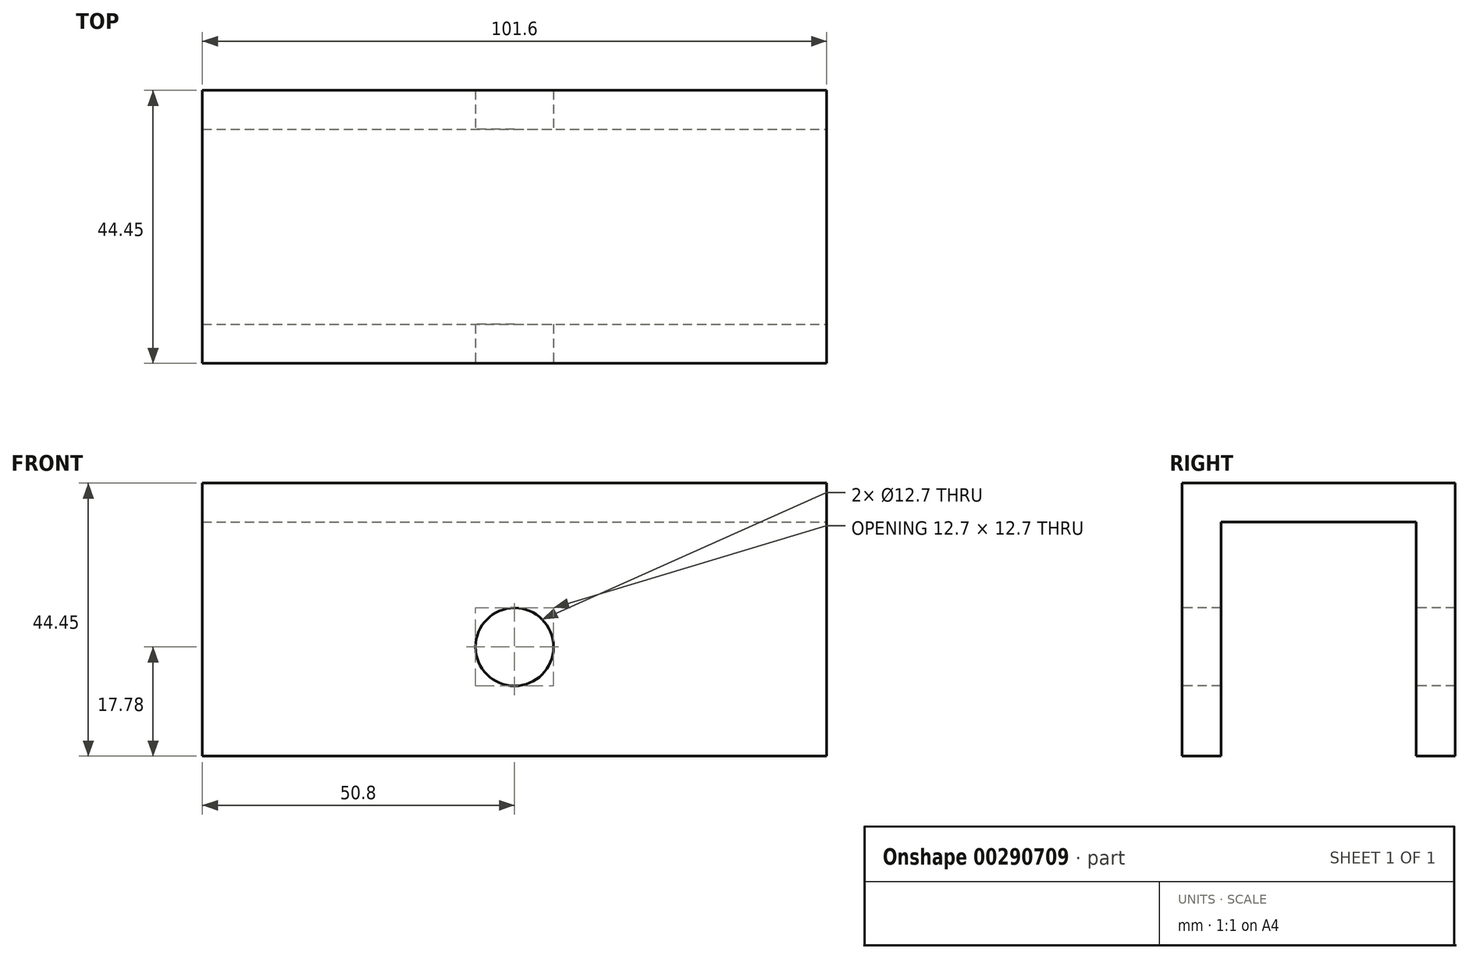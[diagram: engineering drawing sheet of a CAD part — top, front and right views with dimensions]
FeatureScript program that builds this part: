
annotation { "Feature Type Name" : "Feature", "Feature Type Description" : "" }
export const myFeature = defineFeature(function(context is Context, id is Id, definition is map)
    precondition{}
    {
        {
            var Q0;
            Q0=qCreatedBy(makeId("Front.planeOp"),FACE);
            var sketch = newSketch(context, id + "F0", { "sketchPlane" : qUnion([Q0])});
            skLineSegment(sketch, "E0.bottom", {"start": v(0, 0) * mm, "end": v(101.6, 0) * mm});
            skLineSegment(sketch, "E0.top", {"start": v(0, -44.45) * mm, "end": v(101.6, -44.45) * mm});
            skLineSegment(sketch, "E0.left", {"start": v(0, 0) * mm, "end": v(0, -44.45) * mm});
            skLineSegment(sketch, "E0.right", {"start": v(101.6, 0) * mm, "end": v(101.6, -44.45) * mm});
            skSolve(sketch);
        }
        {
            var Q0;
            Q0=makeQuery(id+"F0.imprint","IMPRINT",FACE,{"disambiguationData":[TD([[makeQuery(id+"F0.imprint","IMPRINT",EDGE,{"derivedFrom":sQuery(id+"F0.wireOp",EDGE,"E0.bottom")}),-1.0]])]});
            extrude(context, id + "F1", {"entities" : qUnion([Q0]), "depth" : 44.45 * mm});
        }
        {
            var Q0;
            Q0=makeQuery(id+"F1.opExtrude","SWEPT_FACE",FACE,{"disambiguationData":[OSD([sQuery(id+"F0.wireOp",EDGE,"E0.right")])]});
            var sketch = newSketch(context, id + "F2", { "sketchPlane" : qUnion([Q0])});
            skLineSegment(sketch, "E1.bottom", {"start": v(-38.1, -44.45) * mm, "end": v(-6.35, -44.45) * mm});
            skLineSegment(sketch, "E1.top", {"start": v(-38.1, -6.35) * mm, "end": v(-6.35, -6.35) * mm});
            skLineSegment(sketch, "E1.left", {"start": v(-38.1, -44.45) * mm, "end": v(-38.1, -6.35) * mm});
            skLineSegment(sketch, "E1.right", {"start": v(-6.35, -44.45) * mm, "end": v(-6.35, -6.35) * mm});
            skSolve(sketch);
        }
        {
            var Q0;
            Q0=makeQuery(id+"F2.imprint","IMPRINT",FACE,{"disambiguationData":[TD([[makeQuery(id+"F2.imprint","IMPRINT",EDGE,{"derivedFrom":sQuery(id+"F2.wireOp",EDGE,"E1.bottom")}),1.0]])]});
            extrude(context, id + "F3", {"entities" : qUnion([Q0]), "operationType" : NewBodyOperationType.REMOVE, "endBound" : BoundingType.THROUGH_ALL, "oppositeDirection" : true, "depth" : 25.4 * mm});
        }
        {
            var Q0;
            Q0=makeQuery(id+"F1.opExtrude","CAP_FACE",FACE,{"disambiguationData":[OSD([sQuery(id+"F0.wireOp",EDGE,"E0.bottom"),sQuery(id+"F0.wireOp",EDGE,"E0.top"),sQuery(id+"F0.wireOp",EDGE,"E0.left"),sQuery(id+"F0.wireOp",EDGE,"E0.right")])],"isStart":false});
            var sketch = newSketch(context, id + "F4", { "sketchPlane" : qUnion([Q0])});
            skCircle(sketch, "E2", {"center": v(50.8, -26.67) * mm, "radius": 6.35 * mm});
            skSolve(sketch);
        }
        {
            var Q0;
            Q0=makeQuery(id+"F4.imprint","IMPRINT",FACE,{"disambiguationData":[TD([[makeQuery(id+"F4.imprint","IMPRINT",EDGE,{"derivedFrom":sQuery(id+"F4.wireOp",EDGE,"E2")}),1.0]])]});
            extrude(context, id + "F5", {"entities" : qUnion([Q0]), "operationType" : NewBodyOperationType.REMOVE, "endBound" : BoundingType.THROUGH_ALL, "oppositeDirection" : true, "depth" : 25.4 * mm});
        }
    });
